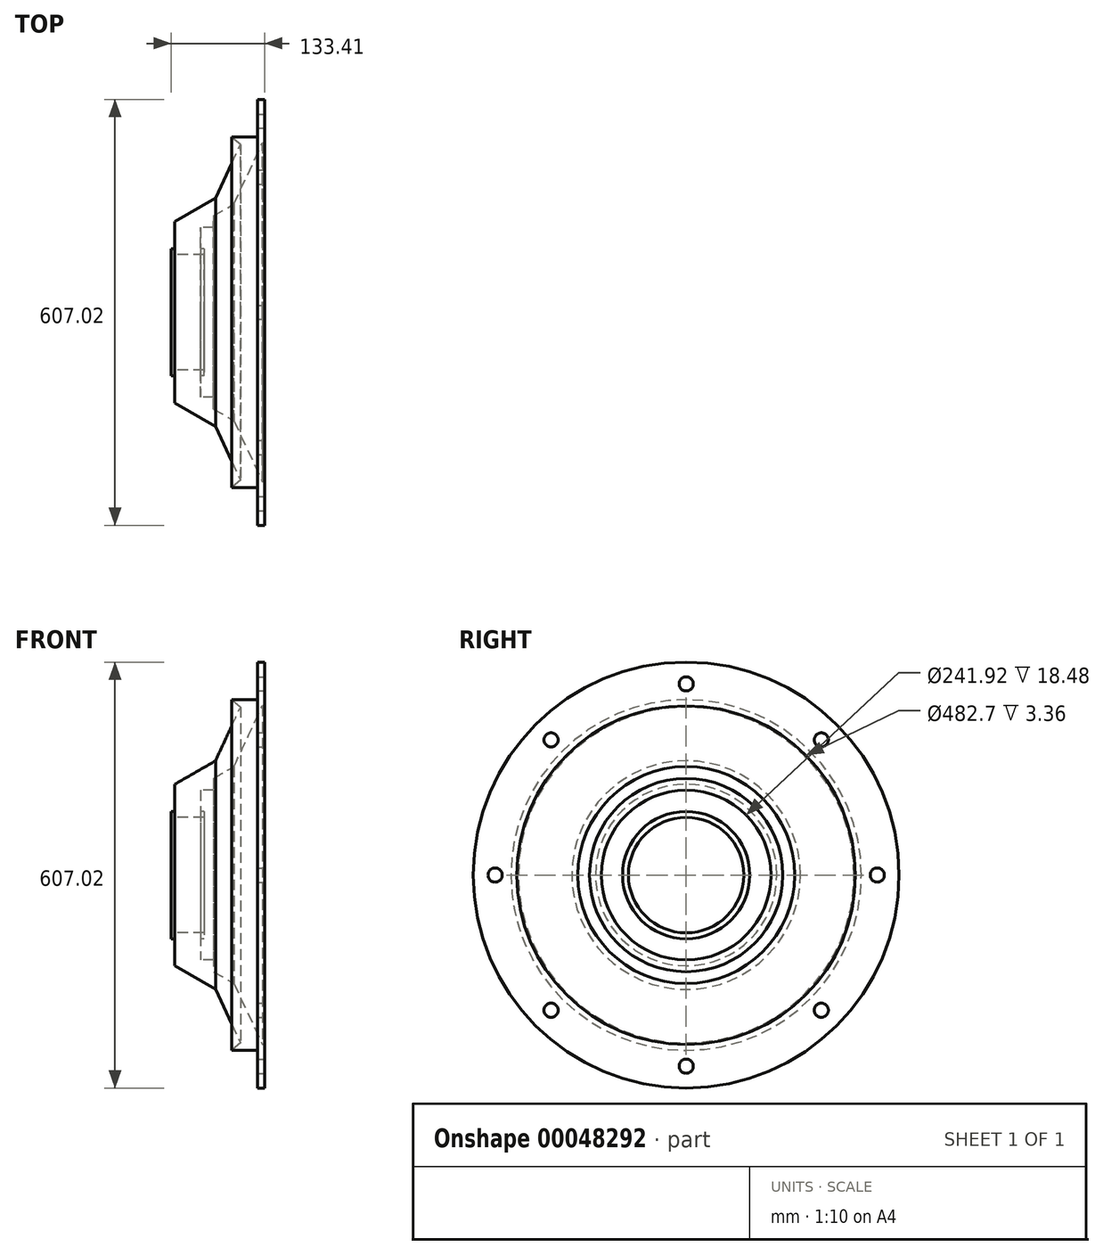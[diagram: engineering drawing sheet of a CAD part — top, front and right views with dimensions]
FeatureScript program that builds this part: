
annotation { "Feature Type Name" : "Feature", "Feature Type Description" : "" }
export const myFeature = defineFeature(function(context is Context, id is Id, definition is map)
    precondition{}
    {
        {
            var Q0;
            Q0=qCreatedBy(makeId("Front.planeOp"),FACE);
            var sketch = newSketch(context, id + "F0", { "sketchPlane" : qUnion([Q0])});
            skLineSegment(sketch, "E0", {"start": v(-82.22, 0) * mm, "end": v(82.22, 0) * mm, "construction": true});
            skLineSegment(sketch, "E1", {"start": v(0, 0) * mm, "end": v(0, 82.32) * mm, "construction": true});
            skLineSegment(sketch, "E2", {"start": v(0, 82.32) * mm, "end": v(47.04, 82.32) * mm});
            skLineSegment(sketch, "E3", {"start": v(0, 82.32) * mm, "end": v(0, 90.72) * mm});
            skLineSegment(sketch, "E4", {"start": v(0, 90.72) * mm, "end": v(5.04, 90.72) * mm});
            skLineSegment(sketch, "E5", {"start": v(5.04, 90.72) * mm, "end": v(5.04, 129.36) * mm});
            skLineSegment(sketch, "E6", {"start": v(47.04, 82.32) * mm, "end": v(47.04, 90.72) * mm});
            skLineSegment(sketch, "E7", {"start": v(47.04, 90.72) * mm, "end": v(42, 90.72) * mm});
            skLineSegment(sketch, "E8", {"start": v(42, 90.72) * mm, "end": v(42, 120.96) * mm});
            skLineSegment(sketch, "E9", {"start": v(42, 120.96) * mm, "end": v(60.48, 120.96) * mm});
            skLineSegment(sketch, "E10", {"start": v(60.48, 120.96) * mm, "end": v(60.48, 137.76) * mm});
            skLineSegment(sketch, "E11", {"start": v(60.48, 137.76) * mm, "end": v(161.44, 137.76) * mm, "construction": true});
            skLineSegment(sketch, "E12", {"start": v(60.48, 137.76) * mm, "end": v(89.58, 154.56) * mm});
            skLineSegment(sketch, "E13", {"start": v(5.04, 129.36) * mm, "end": v(63.24, 162.96) * mm});
            skLineSegment(sketch, "E14", {"start": v(89.58, 154.56) * mm, "end": v(130.05, 241.35) * mm});
            skLineSegment(sketch, "E15", {"start": v(63.24, 162.96) * mm, "end": v(98.83, 239.3) * mm});
            skLineSegment(sketch, "E16", {"start": v(130.05, 241.35) * mm, "end": v(133.4, 241.35) * mm});
            skLineSegment(sketch, "E17", {"start": v(133.4, 241.35) * mm, "end": v(133.4, 258.15) * mm});
            skLineSegment(sketch, "E18", {"start": v(123.33, 303.5) * mm, "end": v(123.33, 249.75) * mm});
            skLineSegment(sketch, "E19", {"start": v(123.33, 249.75) * mm, "end": v(86.37, 249.75) * mm});
            skLineSegment(sketch, "E20", {"start": v(86.37, 249.75) * mm, "end": v(98.83, 239.3) * mm});
            skLineSegment(sketch, "E21", {"start": v(123.33, 303.5) * mm, "end": v(133.4, 303.5) * mm});
            skLineSegment(sketch, "E22", {"start": v(133.4, 258.15) * mm, "end": v(133.4, 303.5) * mm});
            skSolve(sketch);
        }
        {
            var Q0;
            Q0=makeQuery(id+"F0.imprint","IMPRINT",FACE,{"disambiguationData":[TD([[makeQuery(id+"F0.imprint","IMPRINT",EDGE,{"derivedFrom":sQuery(id+"F0.wireOp",EDGE,"E2")}),1.0]])]});
            var Q1;
            Q1=sQuery(id+"F0.wireOp",EDGE,"E0");
            revolve(context, id + "F1", {"entities" : qUnion([Q0]), "axis" : qUnion([Q1]), "revolveType" : RevolveType.FULL});
        }
        {
            var Q0;
            Q0=makeQuery(id+"F1.opRevolve","SWEPT_FACE",FACE,{"disambiguationData":[OSD([sQuery(id+"F0.wireOp",EDGE,"E17"),sQuery(id+"F0.wireOp",EDGE,"E22")])]});
            var sketch = newSketch(context, id + "F2", { "sketchPlane" : qUnion([Q0])});
            skLineSegment(sketch, "E23", {"start": v(0, 0) * mm, "end": v(0, 321.49) * mm, "construction": true});
            skLineSegment(sketch, "E24", {"start": v(0, 303.5) * mm, "end": v(0, 241.35) * mm});
            skCircle(sketch, "E25", {"center": v(0, 272.43) * mm, "radius": 10.08 * mm});
            skCircle(sketch, "E26.1.0", {"center": v(-192.64, 192.64) * mm, "radius": 10.08 * mm});
            skCircle(sketch, "E26.2.0", {"center": v(-272.43, 0) * mm, "radius": 10.08 * mm});
            skPoint(sketch, "E26.center", {"position": v(0, 0) * mm});
            skCircle(sketch, "E27.1.3.0", {"center": v(-192.64, -192.64) * mm, "radius": 10.08 * mm});
            skCircle(sketch, "E27.1.4.0", {"center": v(0, -272.43) * mm, "radius": 10.08 * mm});
            skCircle(sketch, "E27.1.5.0", {"center": v(192.64, -192.64) * mm, "radius": 10.08 * mm});
            skCircle(sketch, "E27.1.6.0", {"center": v(272.43, 0) * mm, "radius": 10.08 * mm});
            skCircle(sketch, "E27.1.7.0", {"center": v(192.64, 192.64) * mm, "radius": 10.08 * mm});
            skSolve(sketch);
        }
        {
            var Q0;
            Q0=sQuery(id+"F2.wireOp",VERTEX,"E25.center");
            var Q1;
            Q1=sQuery(id+"F2.wireOp",VERTEX,"E26.1.0.center");
            var Q2;
            Q2=sQuery(id+"F2.wireOp",VERTEX,"E26.2.0.center");
            var Q3;
            Q3=sQuery(id+"F2.wireOp",VERTEX,"E27.1.7.0.center");
            var Q4;
            Q4=sQuery(id+"F2.wireOp",VERTEX,"E27.1.6.0.center");
            var Q5;
            Q5=sQuery(id+"F2.wireOp",VERTEX,"E27.1.3.0.center");
            var Q6;
            Q6=sQuery(id+"F2.wireOp",VERTEX,"E27.1.4.0.center");
            var Q7;
            Q7=sQuery(id+"F2.wireOp",VERTEX,"E27.1.5.0.center");
            var Q8;
            Q8=makeQuery(id+"F1.opRevolve","SWEPT_BODY",BODY,{"disambiguationData":[OSD([sQuery(id+"F0.wireOp",EDGE,"E2"),sQuery(id+"F0.wireOp",EDGE,"E3"),sQuery(id+"F0.wireOp",EDGE,"E4"),sQuery(id+"F0.wireOp",EDGE,"E5"),sQuery(id+"F0.wireOp",EDGE,"E6"),sQuery(id+"F0.wireOp",EDGE,"E7"),sQuery(id+"F0.wireOp",EDGE,"E8"),sQuery(id+"F0.wireOp",EDGE,"E9"),sQuery(id+"F0.wireOp",EDGE,"E10"),sQuery(id+"F0.wireOp",EDGE,"E12"),sQuery(id+"F0.wireOp",EDGE,"E13"),sQuery(id+"F0.wireOp",EDGE,"E14"),sQuery(id+"F0.wireOp",EDGE,"E15"),sQuery(id+"F0.wireOp",EDGE,"E16"),sQuery(id+"F0.wireOp",EDGE,"E17"),sQuery(id+"F0.wireOp",EDGE,"E18"),sQuery(id+"F0.wireOp",EDGE,"E19"),sQuery(id+"F0.wireOp",EDGE,"E20"),sQuery(id+"F0.wireOp",EDGE,"E21"),sQuery(id+"F0.wireOp",EDGE,"E22")])]});
            hole(context, id + "F3", {"style" : HoleStyle.SIMPLE, "holeDiameter" : 20.16 * mm, "endStyle" : HoleEndStyle.THROUGH, "locations" : qUnion([Q0, Q1, Q2, Q3, Q4, Q5, Q6, Q7]), "scope" : qUnion([Q8])});
        }
    });
